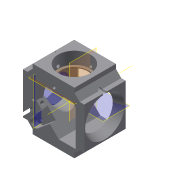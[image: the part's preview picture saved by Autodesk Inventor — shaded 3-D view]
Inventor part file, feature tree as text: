
AUTODESK INVENTOR PART (.ipt)
format: ipt  version: 2022 (Build 260153000, 153)  size: 466,944 bytes
history: native  units: mm
features: extrude x15, sketch x15, reference x15, other x14, plane x7, projected_geometry x6, pattern_circular x2, hole x1
ambient origin geometry x8: Origin, YZ Plane, XZ Plane, XY Plane, X Axis, Y Axis, Z Axis, Center Point
bodies: Solid1 (feature_tree)
feature tree (75):
  plane  "Work Plane1"
  extrude  "Extrusion1"  Depth=33.8mm
  extrude  "IM_offset"  Depth=53.8mm
  plane  "Arbeitsebene12"
  plane  "Arbeitsebene13"
  sketch  "Skizze39"  dims[d21=45.0mm d22=45.0mm]
  plane  "Arbeitsebene14"
  extrude  "Extrusion34"  Depth=45.0mm
  extrude  "Extrusion35"  Depth=20.0mm
  extrude  "Extrusion36"  Depth=2.8mm
  extrude  "Extrusion37"  Depth=3.0mm
  extrude  "Extrusion38"  Depth=0.1mm
  extrude  "Extrusion39"  Depth=0.1mm
  plane  "Arbeitsebene15"
  plane  "Arbeitsebene16"
  extrude  "Extrusion41"  Depth=10.0mm TaperAngle=0.0deg
  plane  "Arbeitsebene17"
  extrude  "Extrusion42"  Depth=11.1mm TaperAngle=0.0deg
  extrude  "Extrusion43"  TaperAngle=0.0deg  [1 undecoded]
  pattern_circular  "Runde Anordnung2"  Count=2  [1 undecoded]
  other  "Arbeitsachse1"
  pattern_circular  "Runde Anordnung3"  Count=3  [1 undecoded]
  hole  "Bohrung3"  [1 undecoded]
  extrude  "Extrusion45"  Depth=32.0mm
  extrude  "Extrusion46"  Depth=5.0mm
  extrude  "Extrusion47"  Depth=5.0mm
  extrude  "Extrusion48"  Depth=5.0mm
  sketch  "Sketch1"  dims[d10=33.8mm d11=0.0mm d18=53.8mm]
  reference  "Reference1"
  reference  "Reference2"
  reference  "Reference3"
  reference  "Reference4"
  reference  "Reference9"
  reference  "Reference20"
  reference  "Reference21"
  reference  "Reference22"
  reference  "Reference23"
  reference  "Reference24"
  sketch  "Skizze4"  dims[d19=45.0deg d20=53.8mm]
  projected_geometry  "Projizierte Kontur1"
  reference  "Referenz29"
  reference  "Referenz30"
  sketch  "Skizze40"  dims[d30=20.0mm d31=20.0mm]
  reference  "Referenz31"
  sketch  "Skizze41"  dims[d32=2.8mm d33=2.8mm]
  projected_geometry  "Projizierte Kontur24"
  reference  "Referenz32"
  sketch  "Skizze42"  dims[d34=2.8mm d35=3.0mm]
  sketch  "Skizze46"  dims[d36=0.1mm d37=0.1mm]
  sketch  "Skizze48"  dims[d38=0.1mm d39=0.1mm]
  sketch  "Skizze49"  dims[d40=0.2mm d41=10.0mm d42=0.0mm]
  sketch  "Skizze51"  dims[d196=11.1mm d197=0.0mm d199=11.1mm d200=0.0mm]
  sketch  "Skizze52"  dims[d201=20.0mm d202=0.0mm d203=0.0mm d204=20.0mm]
  projected_geometry  "Projizierte Kontur25"
  projected_geometry  "Projizierte Kontur26"
  sketch  "Skizze54"  dims[d205=14.0mm d206=0.0mm d230=30.0mm d231=0.0mm]
  sketch  "Skizze55"  dims[d232=16.0mm d233=-3.490659mm d234=30.0mm]
  projected_geometry  "Projizierte Kontur27"
  reference  "Referenz39"
  sketch  "Skizze56"  dims[d241=32.0mm d242=32.0mm]
  sketch  "Skizze57"  dims[d243=7.0mm d244=7.0mm d251=2.8mm d252=6.0mm d253=6.0mm d254=10.0mm d255=90.0deg d256=20.0mm d257=20.594885mm d258=26.3mm d259=26.3mm d260=-10.0mm d261=-10.0mm d262=22.0mm d263=10.0mm d264=0.0mm d265=-10.0mm d266=22.0mm d267=10.0mm d268=0.0mm d269=2.9mm d270=20.0mm d271=0.0mm d272=40.0mm d273=360.0deg d275=20.0mm d276=90.0deg d283=1.806957mm d284=45.0deg d285=13.0mm d286=14.0mm d287=14.0mm d288=0.0mm d289=13.0mm d290=8.0mm d291=0.0mm d292=10.0mm d293=0.0mm d294=2.8mm d295=0.0mm d296=0.0mm d297=5.0mm d298=0.0mm d299=6.981317mm d300=24.43461mm d301=5.0mm d302=0.0mm]
  projected_geometry  "Projizierte Kontur28"
  other  "Assembly_Cube_v2_Thorlabs.iam"
  other  "10_Cube_Base:1"
  other  "00_Base_v0:1"
  other  "Assembly_Cube_Kinematic_Mirrormount_v2.iam"
  other  "Assembly_Cube_empty_1x1_v2:1"
  other  "10_Cube_1x1_v2:1"
  other  "10_Lid_1x1_v2:1"
  other  "Assembly_Cube_Fibercombiner_v3.iam"
  other  "00_30126G3-Step:2"
  other  "00_Thorlabs_Cage_CP33_M:1"
  other  "00_SM1FC-Step:1"
  other  "20_Cube_Insert_Fibercombiner_FPC_filtermount_v3:1"
  other  "10_Cube_Lid:1"
note: 4 required parameter values undecoded (feature->parameter linkage not recoverable at this tier; creation-order binding heuristic only, values carry confidence <= 0.55)
